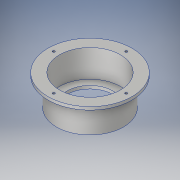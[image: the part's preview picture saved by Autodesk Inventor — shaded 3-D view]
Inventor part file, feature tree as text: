
AUTODESK INVENTOR PART (.ipt)
format: ipt  version: 2018 (Build 220112000, 112)  size: 145,408 bytes
history: native  units: in
note: dims shown in document units (in); Inventor stores cm internally (conversion verified against a paired STEP export)
features: sketch x5, extrude x4, thread x4, hole x1
ambient origin geometry x8: Origin, YZ Plane, XZ Plane, XY Plane, X Axis, Y Axis, Z Axis, Center Point
bodies: Solid1 (feature_tree)
feature tree (14):
  extrude  "Extrusion1"  Depth=1.5748in TaperAngle=0.0deg
  extrude  "Extrusion2"  Depth=1.4173in TaperAngle=0.0deg
  extrude  "Extrusion3"  Depth=1.4173in TaperAngle=0.0deg
  extrude  "Extrusion4"  Depth=1.4173in TaperAngle=0.0deg
  hole  "Hole1"  [1 undecoded]
  thread  "Thread1"  [1 undecoded]
  thread  "Thread2"  [1 undecoded]
  thread  "Thread3"  [1 undecoded]
  thread  "Thread4"  [1 undecoded]
  sketch  "Sketch1"  dims[d0=4.3307in d1=1.5748in d2=0.0in]
  sketch  "Sketch2"  dims[d3=3.4646in d4=1.4173in d5=0.0in]
  sketch  "Sketch3"  dims[d6=2.3622in d7=1.4173in d8=0.0in]
  sketch  "Sketch4"  dims[d9=3.1496in d10=1.4173in d11=0.0in]
  sketch  "Sketch5"  dims[d12=3.7402in d13=0.1575in d14=1.5748in d16=360.0deg d18=0.1181in d19=0.2362in d20=0.1575in d21=0.0787in d22=90.0deg d23=0.315in d24=0.8108in d25=0.3937in d26=0.0in d27=0.3937in d28=0.0in d29=0.3937in d30=0.0in d31=0.3937in d32=0.0in]
note: 5 required parameter values undecoded (feature->parameter linkage not recoverable at this tier; creation-order binding heuristic only, values carry confidence <= 0.55)
